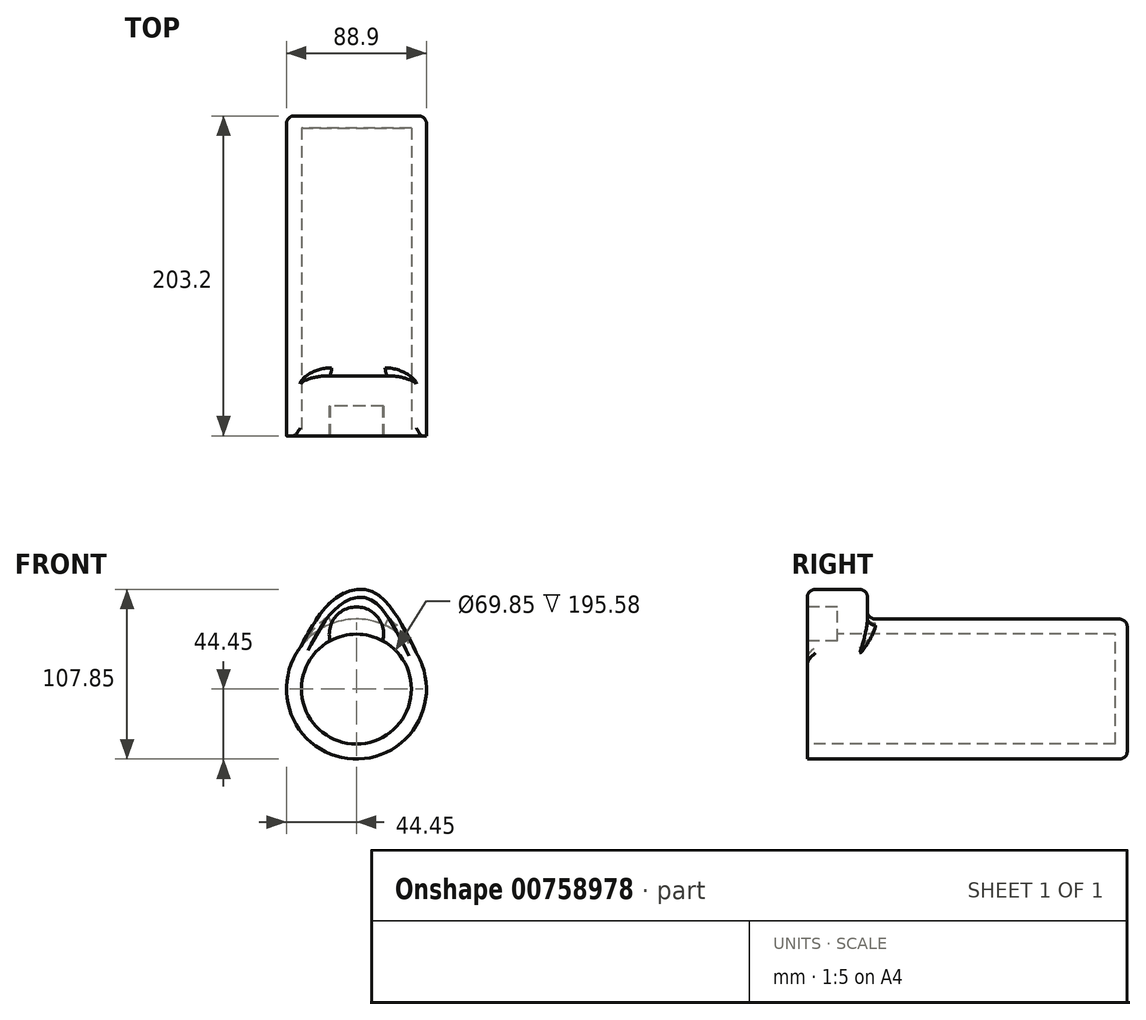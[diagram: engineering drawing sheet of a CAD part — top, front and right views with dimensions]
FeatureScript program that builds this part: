
annotation { "Feature Type Name" : "Feature", "Feature Type Description" : "" }
export const myFeature = defineFeature(function(context is Context, id is Id, definition is map)
    precondition{}
    {
        {
            var Q0;
            Q0=qCreatedBy(makeId("Front.planeOp"),FACE);
            var sketch = newSketch(context, id + "F0", { "sketchPlane" : qUnion([Q0])});
            skCircle(sketch, "E0", {"center": v(0, 0) * mm, "radius": 44.45 * mm});
            skSolve(sketch);
        }
        {
            var Q0;
            Q0=makeQuery(id+"F0.imprint","IMPRINT",FACE,{"disambiguationData":[TD([[makeQuery(id+"F0.imprint","IMPRINT",EDGE,{"derivedFrom":sQuery(id+"F0.wireOp",EDGE,"E0")}),1.0]])]});
            extrude(context, id + "F1", {"entities" : qUnion([Q0]), "depth" : 203.2 * mm, "offsetDistance" : 25.4 * mm});
        }
        {
            var Q0;
            Q0=makeQuery(id+"F1.opExtrude","CAP_FACE",FACE,{"disambiguationData":[OSD([sQuery(id+"F0.wireOp",EDGE,"E0")])],"isStart":false});
            var sketch = newSketch(context, id + "F2", { "sketchPlane" : qUnion([Q0])});
            skCircle(sketch, "E1", {"center": v(0, 0) * mm, "radius": 34.92 * mm});
            skSolve(sketch);
        }
        {
            var Q0;
            Q0=makeQuery(id+"F2.imprint","IMPRINT",FACE,{"disambiguationData":[TD([[makeQuery(id+"F2.imprint","IMPRINT",EDGE,{"derivedFrom":sQuery(id+"F2.wireOp",EDGE,"E1")}),1.0]])]});
            extrude(context, id + "F3", {"entities" : qUnion([Q0]), "operationType" : NewBodyOperationType.REMOVE, "oppositeDirection" : true, "depth" : 195.58 * mm, "offsetDistance" : 25.4 * mm});
        }
        {
            var Q0;
            Q0=makeQuery(id+"F1.opExtrude","CAP_FACE",FACE,{"disambiguationData":[OSD([sQuery(id+"F0.wireOp",EDGE,"E0")])],"isStart":false});
            var sketch = newSketch(context, id + "F4", { "sketchPlane" : qUnion([Q0])});
            skFitSpline(sketch, "E2", {"points": [v(38.03, 23) * mm, v(11.17, 61.4) * mm, v(-13.17, 57.8) * mm, v(-35.5, 26.75) * mm], "startDerivative": vector(-63.54, 130.37) * mm, "endDerivative": vector(-56.96, -105.93) * mm});
            skSolve(sketch);
        }
        {
            var Q0;
            {var subQ0=sQuery(id+"F4.wireOp",EDGE,"E2");Q0=makeQuery(id+"F4.imprint","IMPRINT",FACE,{"disambiguationData":[TD([[makeQuery(id+"F4.imprint","IMPRINT",EDGE,{"derivedFrom":subQ0}),1.0]])]});}
            extrude(context, id + "F5", {"entities" : qUnion([Q0]), "operationType" : NewBodyOperationType.ADD, "oppositeDirection" : true, "depth" : 38.1 * mm, "offsetDistance" : 25.4 * mm});
        }
        {
            var Q0;
            Q0=makeQuery(id+"F5.opExtrude","CAP_FACE",FACE,{"disambiguationData":[OSD([sQuery(id+"F0.wireOp",EDGE,"E0"),sQuery(id+"F4.wireOp",EDGE,"E2")])],"isStart":false});
            fillet(context, id + "F6", {"entities" : qUnion([Q0]), "radius" : 5.08 * mm, "tangentPropagation" : true, "allowEdgeOverflow" : false});
        }
        {
            var Q0;
            Q0=makeQuery(id+"F5.opExtrude","CAP_FACE",FACE,{"disambiguationData":[OSD([sQuery(id+"F0.wireOp",EDGE,"E0"),sQuery(id+"F4.wireOp",EDGE,"E2")])],"isStart":false});
            var Q1;
            Q1=makeQuery(id+"F5.opExtrude","SWEPT_FACE",FACE,{"disambiguationData":[OSD([sQuery(id+"F4.wireOp",EDGE,"E2")])]});
            fillet(context, id + "F7", {"entities" : qUnion([Q0, Q1]), "radius" : 5.08 * mm, "tangentPropagation" : true, "allowEdgeOverflow" : false});
        }
        {
            var Q0;
            Q0=makeQuery(id+"F1.opExtrude","CAP_EDGE",EDGE,{"disambiguationData":[OSD([sQuery(id+"F0.wireOp",EDGE,"E0")])],"isStart":true});
            fillet(context, id + "F8", {"entities" : qUnion([Q0]), "radius" : 5.08 * mm, "tangentPropagation" : true, "allowEdgeOverflow" : false});
        }
        {
            var Q0;
            {var subQ0=sQuery(id+"F0.wireOp",EDGE,"E0");Q0=makeQuery(id+"F5.boolean.opBoolean","MERGE",FACE,{"derivedFrom":[makeQuery(id+"F1.opExtrude","CAP_FACE",FACE,{"disambiguationData":[OSD([subQ0])],"isStart":false}),makeQuery(id+"F5.opExtrude","CAP_FACE",FACE,{"disambiguationData":[OSD([subQ0,sQuery(id+"F4.wireOp",EDGE,"E2")])],"isStart":true})]});}
            var sketch = newSketch(context, id + "F9", { "sketchPlane" : qUnion([Q0])});
            skCircle(sketch, "E3", {"center": v(0, 34.92) * mm, "radius": 17.25 * mm});
            skSolve(sketch);
        }
        {
            var Q0;
            {var subQ0=sQuery(id+"F9.wireOp",EDGE,"E3");var subQ1=makeQuery(id+"F3.boolean.opBoolean","COPY",EDGE,{"derivedFrom":makeQuery(id+"F3.opExtrude","CAP_EDGE",EDGE,{"disambiguationData":[OSD([sQuery(id+"F2.wireOp",EDGE,"E1")])],"isStart":true})});var subQ2=makeQuery(id+"F9.imprint","INTERSECT",VERTEX,{"disambiguationData":[OD(0.0)],"derivedFrom":[subQ1,subQ0]});Q0=makeQuery(id+"F9.imprint","IMPRINT",FACE,{"disambiguationData":[TD([[makeQuery(id+"F9.imprint","IMPRINT",EDGE,{"disambiguationData":[TD([[subQ2,1.0]])],"derivedFrom":subQ0}),1.0]])]});}
            extrude(context, id + "F10", {"entities" : qUnion([Q0]), "operationType" : NewBodyOperationType.REMOVE, "oppositeDirection" : true, "depth" : 19.05 * mm, "offsetDistance" : 25.4 * mm});
        }
    });
